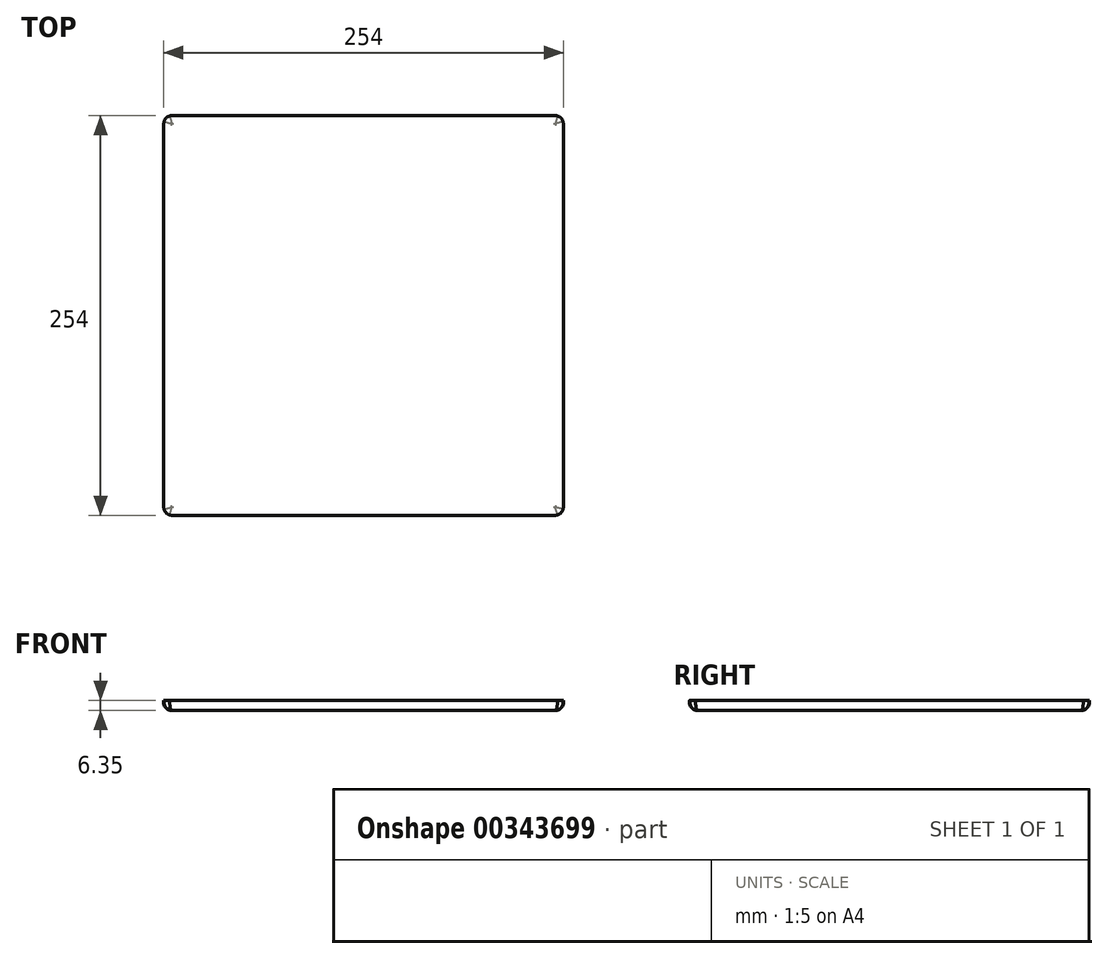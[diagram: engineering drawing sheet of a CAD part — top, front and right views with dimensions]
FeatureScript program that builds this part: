
annotation { "Feature Type Name" : "Feature", "Feature Type Description" : "" }
export const myFeature = defineFeature(function(context is Context, id is Id, definition is map)
    precondition{}
    {
        {
            var Q0;
            Q0=qCreatedBy(makeId("Top.planeOp"),FACE);
            var sketch = newSketch(context, id + "F0", { "sketchPlane" : qUnion([Q0])});
            skLineSegment(sketch, "E0.bottom", {"start": v(127, 127) * mm, "end": v(-127, 127) * mm});
            skLineSegment(sketch, "E0.top", {"start": v(127, -127) * mm, "end": v(-127, -127) * mm});
            skLineSegment(sketch, "E0.left", {"start": v(127, 127) * mm, "end": v(127, -127) * mm});
            skLineSegment(sketch, "E0.right", {"start": v(-127, 127) * mm, "end": v(-127, -127) * mm});
            skPoint(sketch, "E0.middle", {"position": v(0, 0) * mm});
            skSolve(sketch);
        }
        {
            var Q0;
            Q0 = qSketchRegion(id + "F0", true);
            extrude(context, id + "F1", {"entities" : qUnion([Q0]), "depth" : 6.35 * mm});
        }
        {
            var Q0;
            Q0=makeQuery(id+"F1.opExtrude","SWEPT_EDGE",EDGE,{"disambiguationData":[OSD([sQuery(id+"F0.wireOp",EDGE,"E0.bottom"),sQuery(id+"F0.wireOp",EDGE,"E0.right")])]});
            var Q1;
            Q1=makeQuery(id+"F1.opExtrude","SWEPT_EDGE",EDGE,{"disambiguationData":[OSD([sQuery(id+"F0.wireOp",EDGE,"E0.bottom"),sQuery(id+"F0.wireOp",EDGE,"E0.left")])]});
            var Q2;
            Q2=makeQuery(id+"F1.opExtrude","SWEPT_EDGE",EDGE,{"disambiguationData":[OSD([sQuery(id+"F0.wireOp",EDGE,"E0.top"),sQuery(id+"F0.wireOp",EDGE,"E0.left")])]});
            var Q3;
            Q3=makeQuery(id+"F1.opExtrude","SWEPT_EDGE",EDGE,{"disambiguationData":[OSD([sQuery(id+"F0.wireOp",EDGE,"E0.top"),sQuery(id+"F0.wireOp",EDGE,"E0.right")])]});
            fillet(context, id + "F2", {"entities" : qUnion([Q0, Q1, Q2, Q3]), "radius" : 6.35 * mm, "tangentPropagation" : true, "rho" : 0.5, "crossSection" : FilletCrossSection.CONIC, "allowEdgeOverflow" : false});
        }
        {
            var Q0;
            Q0=makeQuery(id+"F1.opExtrude","CAP_EDGE",EDGE,{"disambiguationData":[OSD([sQuery(id+"F0.wireOp",EDGE,"E0.top")])],"isStart":true});
            var Q1;
            Q1=makeQuery(id+"F1.opExtrude","CAP_EDGE",EDGE,{"disambiguationData":[OSD([sQuery(id+"F0.wireOp",EDGE,"E0.left")])],"isStart":true});
            fillet(context, id + "F3", {"entities" : qUnion([Q0, Q1]), "radius" : 5.08 * mm, "tangentPropagation" : true, "allowEdgeOverflow" : false});
        }
    });
